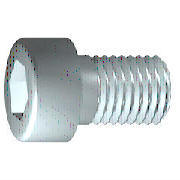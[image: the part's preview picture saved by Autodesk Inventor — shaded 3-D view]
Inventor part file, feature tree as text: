
AUTODESK INVENTOR PART (.ipt)
format: ipt  version: 2018 (Build 220112000, 112)  size: 184,832 bytes
history: native  units: mm (DEFAULTED — no unit token found)
features: sketch x2, extrude x1, plane x1, fillet x1
ambient origin geometry x7: Origin, YZ Plane, XY Plane, X Axis, Y Axis, Z Axis, Center Point
bodies: Solid1 (feature_tree), Body (feature_tree)
feature tree (5):
  extrude  "Slot"  Depth=5.0mm
  plane  "Work Plane1"
  fillet  "Fillet2"  Radius=5.0mm
  sketch  "Sketch1"  dims[d1=22.0mm d2=0.49086mm d3=5.0mm]
  sketch  "Sketch2"  dims[d4=2.5mm d5=60.0deg d6=5.0mm d7=5.0mm d8=4.618802mm d9=8.5mm d10=90.0deg d11=10.0mm d12=0.0mm d13=22.0mm d14=0.0mm d15=0.49076mm d16=0.49076mm d17=0.5mm d19=0.0mm d26=35.0mm d27=45.0deg d28=0.0mm d29=0.0mm d30=0.1mm]
